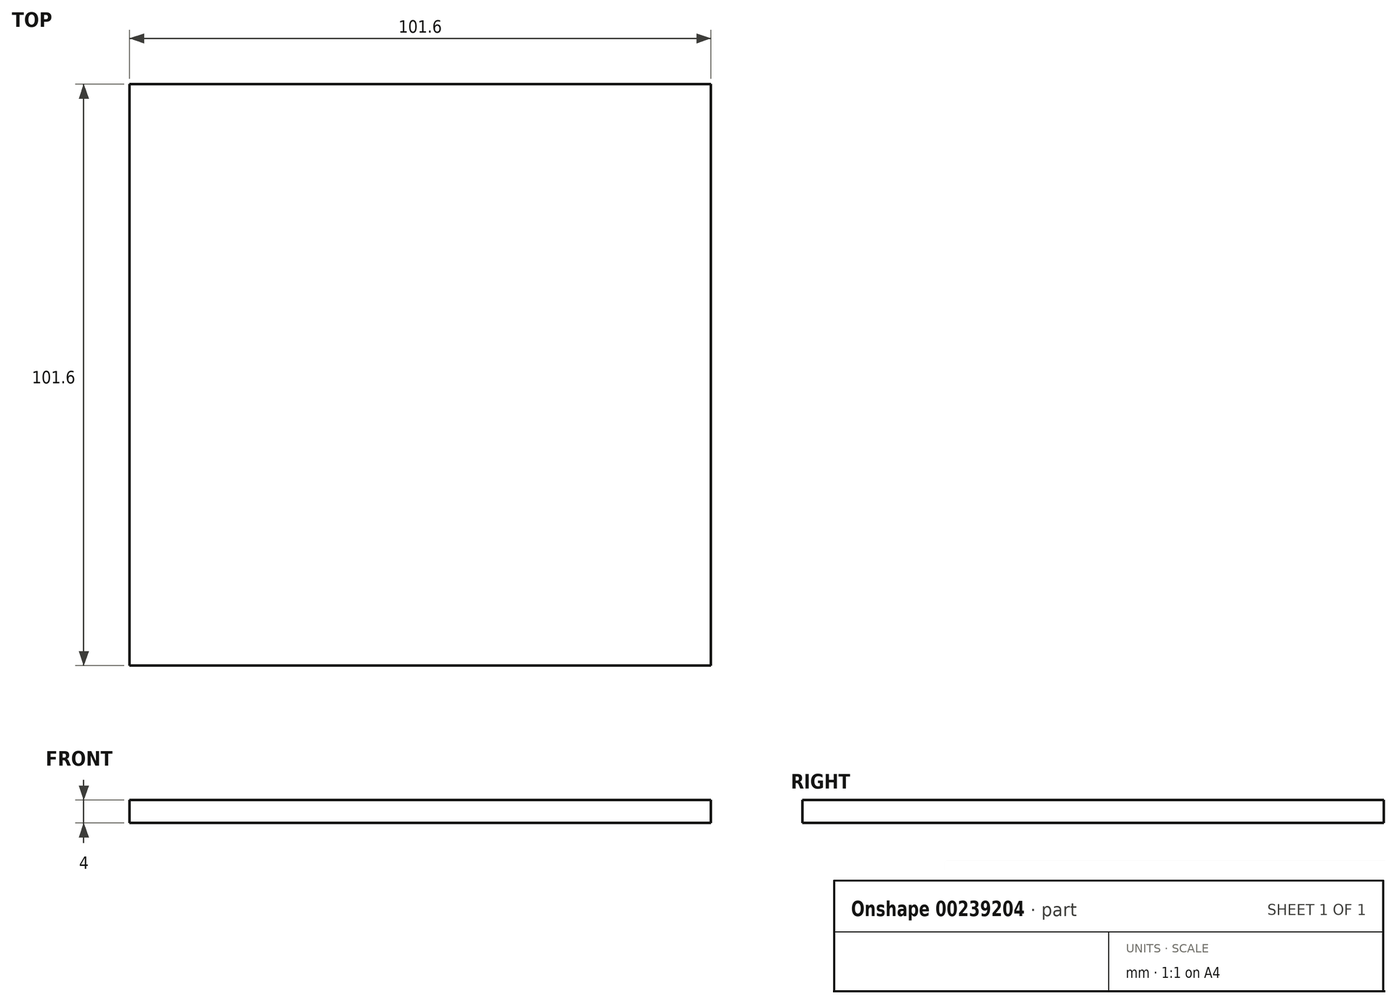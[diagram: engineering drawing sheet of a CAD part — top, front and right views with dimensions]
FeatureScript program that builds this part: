
annotation { "Feature Type Name" : "Feature", "Feature Type Description" : "" }
export const myFeature = defineFeature(function(context is Context, id is Id, definition is map)
    precondition{}
    {
        {
            assignVariable(context, id + "F0", {"name" : "A", "anyValue" : 4});
        }
        {
            var Q0;
            Q0=qCreatedBy(makeId("Top.planeOp"),FACE);
            var sketch = newSketch(context, id + "F1", { "sketchPlane" : qUnion([Q0])});
            skLineSegment(sketch, "E0.bottom", {"start": v(-50.8, 50.8) * mm, "end": v(50.8, 50.8) * mm});
            skLineSegment(sketch, "E0.top", {"start": v(-50.8, -50.8) * mm, "end": v(50.8, -50.8) * mm});
            skLineSegment(sketch, "E0.left", {"start": v(-50.8, 50.8) * mm, "end": v(-50.8, -50.8) * mm});
            skLineSegment(sketch, "E0.right", {"start": v(50.8, 50.8) * mm, "end": v(50.8, -50.8) * mm});
            skSolve(sketch);
        }
        {
            var Q0;
            Q0=makeQuery(id+"F1.imprint","IMPRINT",FACE,{"disambiguationData":[TD([[makeQuery(id+"F1.imprint","IMPRINT",EDGE,{"derivedFrom":sQuery(id+"F1.wireOp",EDGE,"E0.bottom")}),-1.0]])]});
            extrude(context, id + "F2", {"entities" : qUnion([Q0]), "endBound" : BoundingType.SYMMETRIC, "depth" : (getVariable(context, 'A')) * mm});
        }
    });
